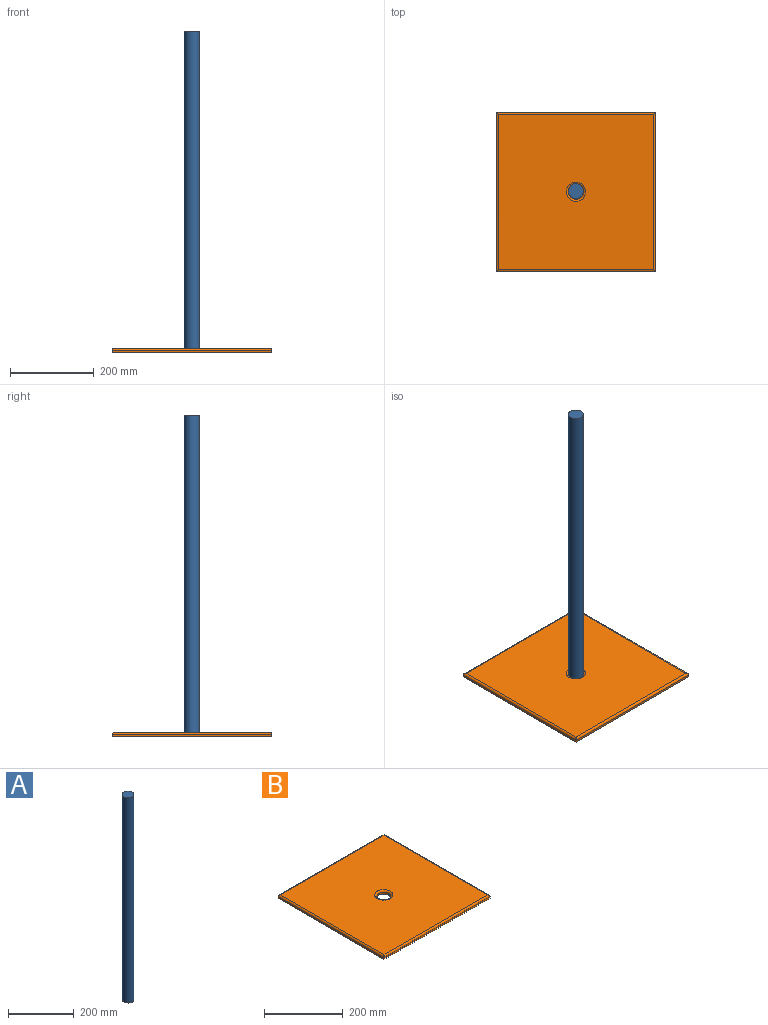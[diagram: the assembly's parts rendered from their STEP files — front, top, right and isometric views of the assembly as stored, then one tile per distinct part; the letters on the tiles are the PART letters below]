
ASSEMBLY  parts=2 mates=1
PART A: 3 faces, bbox 36.1x36.1x762 mm
  f0: cylinder r=18.03mm len=762mm, axis (0,0,-1), area 86343mm2, adj f1,f2
  f1: plane 36.07x36.07mm, normal (0,0,1), area 1021.7mm2, adj f0
  f2: plane 36.07x36.07mm, normal (0,0,-1), area 1021.7mm2, adj f0
PART B: 12 faces, bbox 381x381x10.2 mm
  f0: plane 381x5.08mm, normal (1,0,0), area 1935.5mm2, adj f1,f3,f5,f8
  f1: plane 381x5.08mm, normal (0,1,0), area 1935.5mm2, adj f0,f2,f5,f9
  f2: plane 381x5.08mm, normal (-1,0,0), area 1935.5mm2, adj f1,f3,f5,f11
  f3: plane 381x5.08mm, normal (0,-1,0), area 1935.5mm2, adj f0,f2,f5,f10
  f4: plane 370.84x370.84mm, normal (0,0,1), area 135843.9mm2, adj f7,f8,f9,f10,f11
  f5: plane 381x381mm, normal (0,0,-1), area 144139.3mm2, adj f0,f1,f2,f3,f6
  f6: cylinder r=18.03mm len=36.07mm, axis (0,0,1), area 575.6mm2, adj f5,f7
  f7: torus R=23.11mm, axis (0,0,1), area 996.7mm2, adj f4,f6
  f8: cylinder r=5.08mm len=381mm, axis (0,-1,0), area 3010.8mm2, adj f0,f4,f9,f10
  f9: cylinder r=5.08mm len=381mm, axis (1,0,0), area 3010.8mm2, adj f1,f4,f8,f11
  f10: cylinder r=5.08mm len=381mm, axis (-1,0,0), area 3010.8mm2, adj f3,f4,f8,f11
  f11: cylinder r=5.08mm len=381mm, axis (0,1,0), area 3010.8mm2, adj f2,f4,f9,f10
PLACE A t=(-753.65,-305.66,-186.8)mm
PLACE B t=(-753.4,-306.16,-191.88)mm
MATE fastened B.f6 <-> A.f0  axis (0,0,1) through (-753.65,-305.66,-186.8)mm
